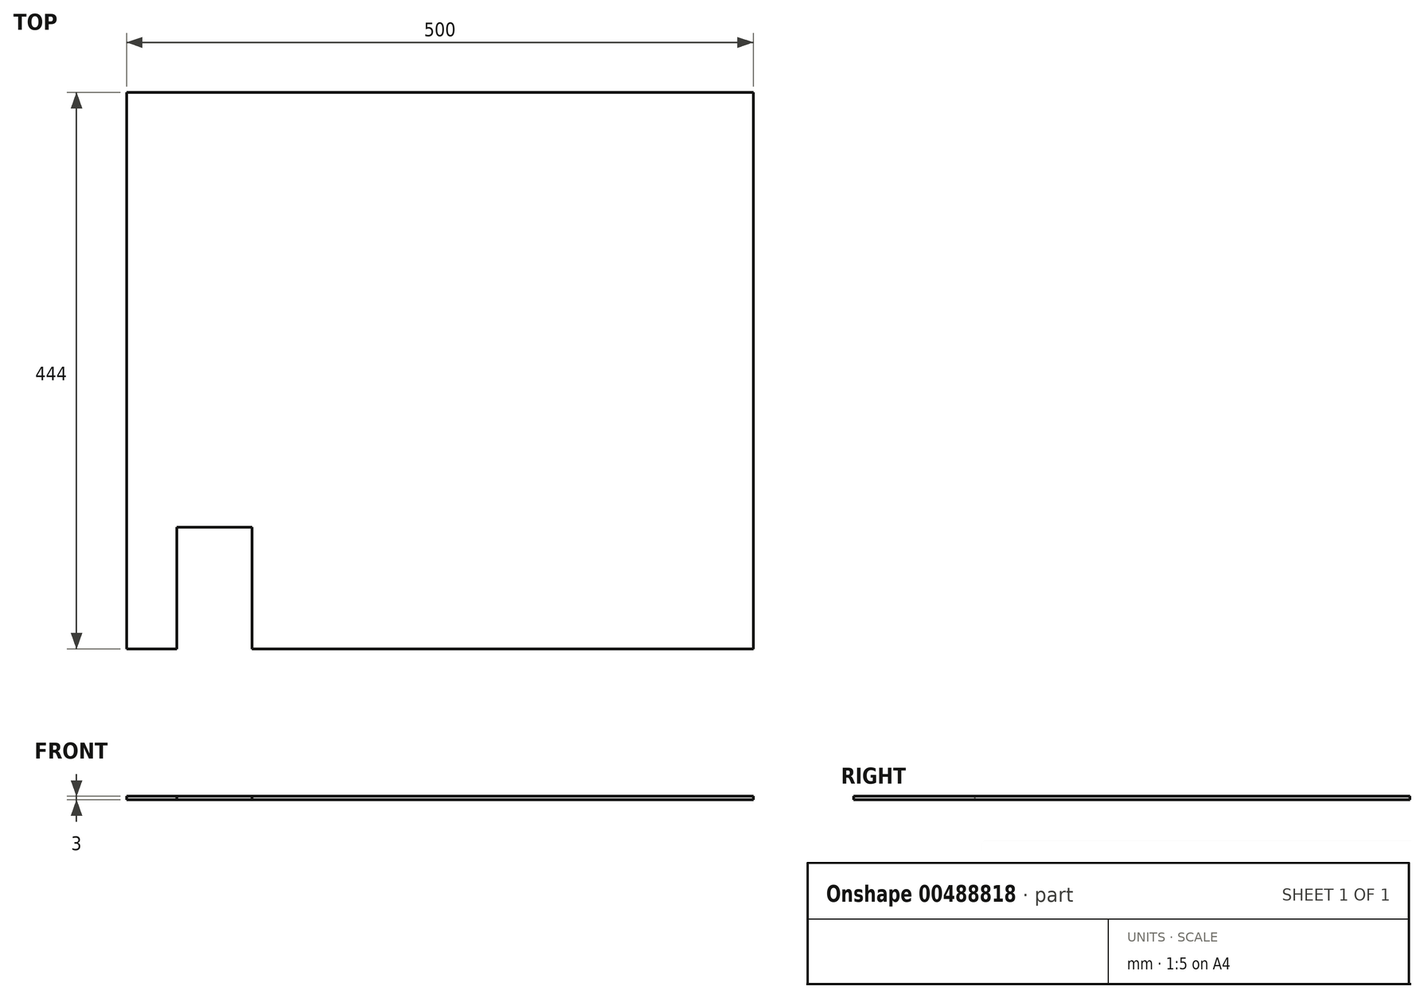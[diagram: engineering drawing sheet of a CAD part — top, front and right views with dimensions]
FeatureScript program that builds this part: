
annotation { "Feature Type Name" : "Feature", "Feature Type Description" : "" }
export const myFeature = defineFeature(function(context is Context, id is Id, definition is map)
    precondition{}
    {
        {
            var Q0;
            Q0=qCreatedBy(makeId("Top.planeOp"),FACE);
            var sketch = newSketch(context, id + "F0", { "sketchPlane" : qUnion([Q0])});
            skLineSegment(sketch, "E0.bottom", {"start": v(-252.84, 310.02) * mm, "end": v(247.16, 310.02) * mm});
            skLineSegment(sketch, "E0.top", {"start": v(-252.84, -133.98) * mm, "end": v(247.16, -133.98) * mm});
            skLineSegment(sketch, "E0.left", {"start": v(-252.84, 310.02) * mm, "end": v(-252.84, -133.98) * mm});
            skLineSegment(sketch, "E0.right", {"start": v(247.16, 310.02) * mm, "end": v(247.16, -133.98) * mm});
            skSolve(sketch);
        }
        {
            var Q0;
            Q0=makeQuery(id+"F0.imprint","IMPRINT",FACE,{"disambiguationData":[TD([[makeQuery(id+"F0.imprint","IMPRINT",EDGE,{"derivedFrom":sQuery(id+"F0.wireOp",EDGE,"E0.bottom")}),-1.0]])]});
            extrude(context, id + "F1", {"entities" : qUnion([Q0]), "depth" : 3 * mm});
        }
        {
            var Q0;
            Q0=makeQuery(id+"F1.opExtrude","CAP_FACE",FACE,{"disambiguationData":[OSD([sQuery(id+"F0.wireOp",EDGE,"E0.bottom"),sQuery(id+"F0.wireOp",EDGE,"E0.top"),sQuery(id+"F0.wireOp",EDGE,"E0.left"),sQuery(id+"F0.wireOp",EDGE,"E0.right")])],"isStart":false});
            var sketch = newSketch(context, id + "F2", { "sketchPlane" : qUnion([Q0])});
            skLineSegment(sketch, "E1", {"start": v(-212.84, -133.98) * mm, "end": v(-212.84, -36.98) * mm});
            skLineSegment(sketch, "E2", {"start": v(-212.84, -36.98) * mm, "end": v(-152.84, -36.98) * mm});
            skLineSegment(sketch, "E3", {"start": v(-152.84, -36.98) * mm, "end": v(-152.84, -133.98) * mm});
            skSolve(sketch);
        }
        {
            var Q0;
            Q0 = qSketchRegion(id + "F2", true);
            var Q1;
            {var subQ0=sQuery(id+"F2.wireOp",EDGE,"E1");Q1=makeQuery(id+"F2.imprint","IMPRINT",FACE,{"disambiguationData":[TD([[makeQuery(id+"F2.imprint","IMPRINT",EDGE,{"derivedFrom":subQ0}),-1.0]])]});}
            extrude(context, id + "F3", {"entities" : qUnion([Q0, Q1]), "operationType" : NewBodyOperationType.REMOVE, "oppositeDirection" : true, "depth" : 25 * mm, "offsetDistance" : 25 * mm});
        }
    });
